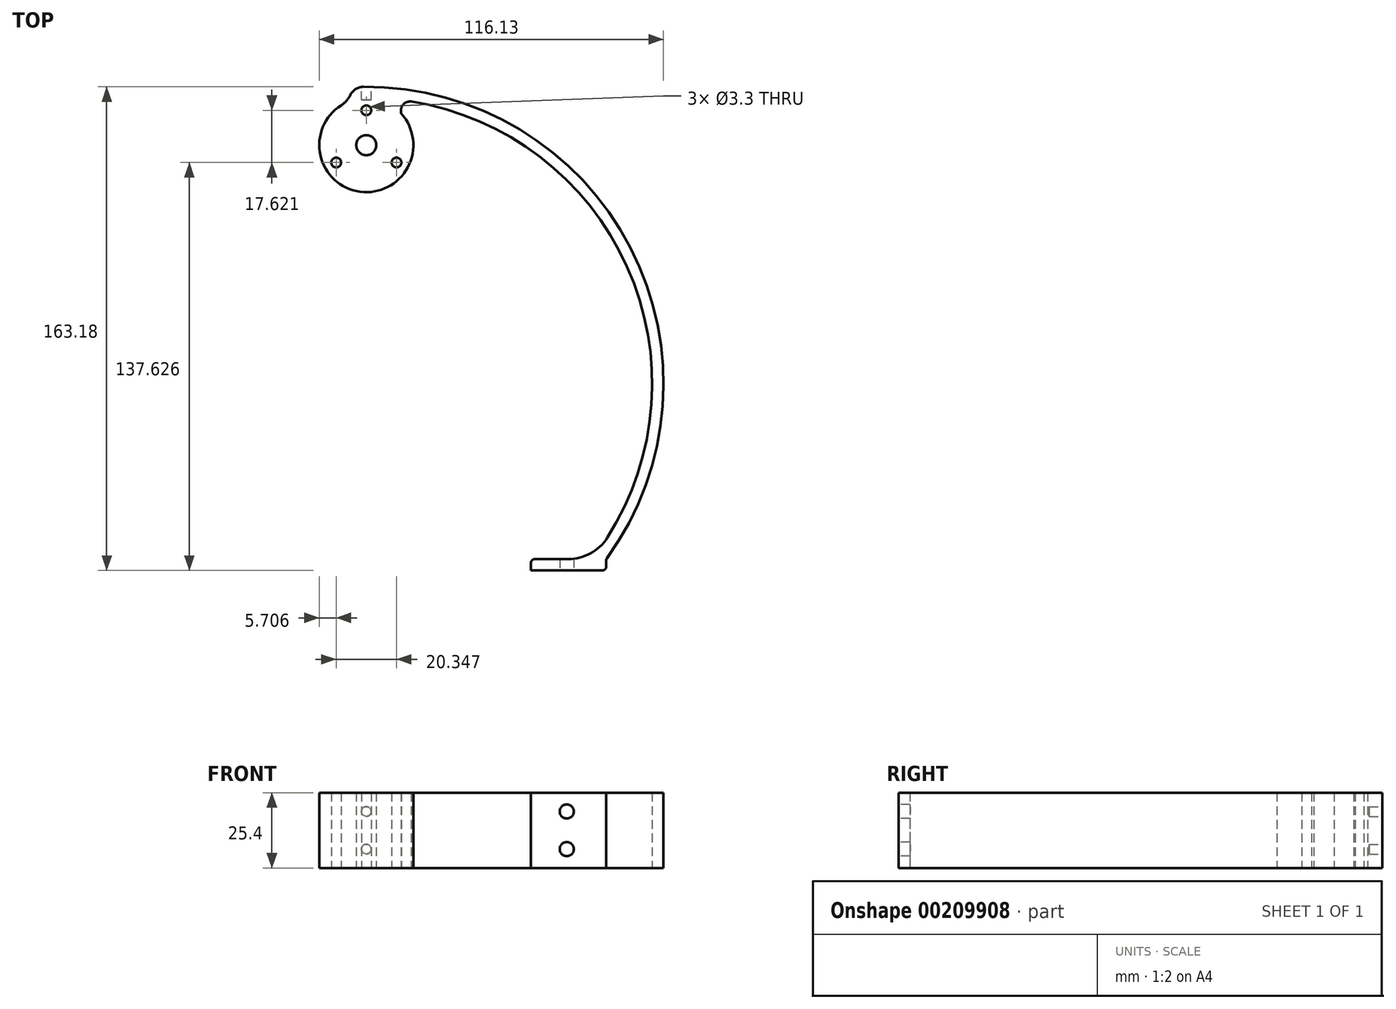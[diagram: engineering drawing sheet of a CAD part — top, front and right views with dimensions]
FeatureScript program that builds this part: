
annotation { "Feature Type Name" : "Feature", "Feature Type Description" : "" }
export const myFeature = defineFeature(function(context is Context, id is Id, definition is map)
    precondition{}
    {
        {
            var Q0;
            Q0=qCreatedBy(makeId("Top.planeOp"),FACE);
            var sketch = newSketch(context, id + "F0", { "sketchPlane" : qUnion([Q0])});
            skCircle(sketch, "E0", {"center": v(0, 0) * mm, "radius": 15.88 * mm});
            skCircle(sketch, "E1", {"center": v(0, 0) * mm, "radius": 3.38 * mm});
            skArc(sketch, "E2", {"start": v(76.2, -139.7) * mm, "mid": v(0, 15.88) * mm, "end": v(-76.2, -139.7) * mm});
            skLineSegment(sketch, "E3", {"start": v(-76.2, -139.7) * mm, "end": v(76.2, -139.7) * mm, "construction": true});
            skLineSegment(sketch, "E4", {"start": v(0, 15.88) * mm, "end": v(0, -139.7) * mm, "construction": true});
            skArc(sketch, "E5.0", {"start": v(81.2, -139.37) * mm, "mid": v(-0.2, 19.67) * mm, "end": v(-80.96, -139.7) * mm});
            skLineSegment(sketch, "E6", {"start": v(56.83, -139.7) * mm, "end": v(80.96, -139.7) * mm, "construction": true});
            skLineSegment(sketch, "E7", {"start": v(76.2, -139.7) * mm, "end": v(55.56, -139.7) * mm});
            skLineSegment(sketch, "E8", {"start": v(55.56, -140.97) * mm, "end": v(55.56, -143.5) * mm});
            skLineSegment(sketch, "E9", {"start": v(55.56, -143.5) * mm, "end": v(79.69, -143.5) * mm});
            skLineSegment(sketch, "E10", {"start": v(80.96, -142.23) * mm, "end": v(80.96, -140.11) * mm});
            skLineSegment(sketch, "E11", {"start": v(0, 19.67) * mm, "end": v(0, 15.88) * mm});
            skLineSegment(sketch, "E12.bottom", {"start": v(0, 26.3) * mm, "end": v(17.78, 26.3) * mm});
            skLineSegment(sketch, "E12.top", {"start": v(0, 22.5) * mm, "end": v(17.78, 22.5) * mm});
            skLineSegment(sketch, "E12.left", {"start": v(0, 26.3) * mm, "end": v(0, 22.5) * mm});
            skLineSegment(sketch, "E12.right", {"start": v(19.05, 25.03) * mm, "end": v(19.05, 23.77) * mm});
            skArc(sketch, "E13", {"start": v(0, 22.5) * mm, "mid": v(-1, 21.09) * mm, "end": v(0, 19.68) * mm});
            skArc(sketch, "E14", {"start": v(0, 26.3) * mm, "mid": v(-4.68, 21.09) * mm, "end": v(0, 15.88) * mm});
            skPoint(sketch, "E15.visualSharp", {"position": v(19.05, 26.3) * mm});
            skArc(sketch, "E15.filletArc", {"start": v(19.05, 25.03) * mm, "mid": v(18.68, 25.93) * mm, "end": v(17.78, 26.3) * mm});
            skPoint(sketch, "E16.visualSharp", {"position": v(19.05, 22.5) * mm});
            skArc(sketch, "E16.filletArc", {"start": v(17.78, 22.5) * mm, "mid": v(18.68, 22.87) * mm, "end": v(19.05, 23.77) * mm});
            skPoint(sketch, "E17.visualSharp", {"position": v(80.96, -143.5) * mm});
            skArc(sketch, "E17.filletArc", {"start": v(79.69, -143.5) * mm, "mid": v(80.58, -143.13) * mm, "end": v(80.96, -142.23) * mm});
            skPoint(sketch, "E18.visualSharp", {"position": v(80.96, -139.7) * mm});
            skArc(sketch, "E18.filletArc", {"start": v(81.2, -139.37) * mm, "mid": v(81.02, -139.72) * mm, "end": v(80.96, -140.11) * mm});
            skPoint(sketch, "E19.newPointB", {"position": v(55.56, -139.7) * mm});
            skArc(sketch, "E19.filletArc", {"start": v(56.83, -139.7) * mm, "mid": v(55.93, -140.07) * mm, "end": v(55.56, -140.97) * mm});
            skLineSegment(sketch, "E20", {"start": v(55.56, -139.7) * mm, "end": v(55.56, -140.97) * mm, "construction": true});
            skLineSegment(sketch, "E21", {"start": v(79.69, -143.5) * mm, "end": v(80.96, -143.5) * mm, "construction": true});
            skLineSegment(sketch, "E22", {"start": v(80.96, -142.23) * mm, "end": v(80.96, -143.5) * mm, "construction": true});
            skArc(sketch, "E23", {"start": v(-8.52, 13.4) * mm, "mid": v(-5.53, 16.7) * mm, "end": v(-4.68, 21.09) * mm});
            skArc(sketch, "E24", {"start": v(15.43, 14.63) * mm, "mid": v(11.9, 12.78) * mm, "end": v(13.1, 8.97) * mm});
            skCircle(sketch, "E25", {"center": v(0, 0) * mm, "radius": 11.75 * mm, "construction": true});
            skCircle(sketch, "E26", {"center": v(0, 11.75) * mm, "radius": 1.65 * mm});
            skCircle(sketch, "E27", {"center": v(10.17, -5.87) * mm, "radius": 1.65 * mm});
            skCircle(sketch, "E28", {"center": v(-10.17, -5.87) * mm, "radius": 1.65 * mm});
            skLineSegment(sketch, "E29", {"start": v(0, 11.75) * mm, "end": v(-10.17, -5.87) * mm, "construction": true});
            skLineSegment(sketch, "E30", {"start": v(10.17, -5.87) * mm, "end": v(0, 11.75) * mm, "construction": true});
            skLineSegment(sketch, "E31", {"start": v(10.17, -5.87) * mm, "end": v(-10.17, -5.87) * mm, "construction": true});
            skLineSegment(sketch, "E32", {"start": v(-10.17, -5.87) * mm, "end": v(5.09, 2.94) * mm, "construction": true});
            skSolve(sketch);
        }
        {
            var Q0;
            {var subQ0=sQuery(id+"F0.wireOp",EDGE,"E24");var subQ1=sQuery(id+"F0.wireOp",EDGE,"E0");var subQ2=makeQuery(id+"F0.imprint","INTERSECT",VERTEX,{"disambiguationData":[OD(0.0)],"derivedFrom":[subQ1,subQ0]});Q0=makeQuery(id+"F0.imprint","IMPRINT",FACE,{"disambiguationData":[TD([[makeQuery(id+"F0.imprint","IMPRINT",EDGE,{"disambiguationData":[TD([[subQ2,-1.0]])],"derivedFrom":subQ1}),1.0]])]});}
            var Q1;
            {var subQ0=sQuery(id+"F0.wireOp",EDGE,"E24");var subQ1=sQuery(id+"F0.wireOp",EDGE,"E2");var subQ2=makeQuery(id+"F0.imprint","INTERSECT",VERTEX,{"disambiguationData":[OD(0.0)],"derivedFrom":[subQ1,subQ0]});Q1=makeQuery(id+"F0.imprint","IMPRINT",FACE,{"disambiguationData":[TD([[makeQuery(id+"F0.imprint","IMPRINT",EDGE,{"disambiguationData":[TD([[subQ2,-1.0]])],"derivedFrom":subQ1}),-1.0]])]});}
            var Q2;
            {var subQ1=sQuery(id+"F0.wireOp",EDGE,"E0");var subQ3=sQuery(id+"F0.wireOp",EDGE,"E24");var subQ4=makeQuery(id+"F0.imprint","INTERSECT",VERTEX,{"disambiguationData":[OD(1.0)],"derivedFrom":[subQ1,subQ3]});Q2=makeQuery(id+"F0.imprint","IMPRINT",FACE,{"disambiguationData":[TD([[makeQuery(id+"F0.imprint","IMPRINT",EDGE,{"disambiguationData":[TD([[subQ4,1.0]])],"derivedFrom":subQ3}),-1.0]])]});}
            var Q3;
            {var subQ1=sQuery(id+"F0.wireOp",EDGE,"E0");var subQ3=sQuery(id+"F0.wireOp",EDGE,"E23");var subQ4=makeQuery(id+"F0.imprint","INTERSECT",VERTEX,{"derivedFrom":[subQ1,subQ3]});Q3=makeQuery(id+"F0.imprint","IMPRINT",FACE,{"disambiguationData":[TD([[makeQuery(id+"F0.imprint","IMPRINT",EDGE,{"disambiguationData":[TD([[subQ4,-1.0]])],"derivedFrom":subQ3}),-1.0]])]});}
            var Q4;
            Q4=makeQuery(id+"F0.imprint","IMPRINT",FACE,{"disambiguationData":[TD([[makeQuery(id+"F0.imprint","IMPRINT",EDGE,{"derivedFrom":sQuery(id+"F0.wireOp",EDGE,"E8")}),1.0]])]});
            var Q5;
            {var subQ3=sQuery(id+"F0.wireOp",EDGE,"E23");var subQ5=sQuery(id+"F0.wireOp",EDGE,"E5.0");var subQ6=makeQuery(id+"F0.imprint","INTERSECT",VERTEX,{"derivedFrom":[subQ5,subQ3]});Q5=makeQuery(id+"F0.imprint","IMPRINT",FACE,{"disambiguationData":[TD([[makeQuery(id+"F0.imprint","IMPRINT",EDGE,{"disambiguationData":[TD([[subQ6,1.0]])],"derivedFrom":subQ5}),1.0]])]});}
            var Q6;
            {var subQ0=sQuery(id+"F0.wireOp",EDGE,"E11");Q6=makeQuery(id+"F0.imprint","IMPRINT",FACE,{"disambiguationData":[TD([[makeQuery(id+"F0.imprint","IMPRINT",EDGE,{"derivedFrom":subQ0}),-1.0]])]});}
            var Q7;
            Q7=makeQuery(id+"F0.imprint","IMPRINT",FACE,{"disambiguationData":[TD([[makeQuery(id+"F0.imprint","IMPRINT",EDGE,{"derivedFrom":sQuery(id+"F0.wireOp",EDGE,"E1")}),-1.0]])]});
            extrude(context, id + "F1", {"entities" : qUnion([Q0, Q1, Q2, Q3, Q4, Q5, Q6, Q7]), "depth" : 25.4 * mm});
        }
        {
            var Q0;
            Q0=qCreatedBy(makeId("Front.planeOp"),FACE);
            cPlane(context, id + "F2", {"entities" : qUnion([Q0]), "cplaneType" : CPlaneType.OFFSET, "offset" : 25.4 * mm, "oppositeDirection" : true, "width" : 152.4 * mm, "height" : 152.4 * mm});
        }
        {
            var Q0;
            Q0=qCreatedBy(id+"F2.planeOp",FACE);
            var sketch = newSketch(context, id + "F3", { "sketchPlane" : qUnion([Q0])});
            skCircle(sketch, "E33", {"center": v(0, 6.35) * mm, "radius": 1.65 * mm});
            skCircle(sketch, "E34", {"center": v(0, 19.05) * mm, "radius": 1.65 * mm});
            skSolve(sketch);
        }
        {
            var Q0;
            Q0 = qSketchRegion(id + "F3", true);
            extrude(context, id + "F4", {"entities" : qUnion([Q0]), "operationType" : NewBodyOperationType.REMOVE, "depth" : 10.16 * mm});
        }
        {
            var Q0;
            Q0=makeQuery(id+"F1.opExtrude","SWEPT_EDGE",EDGE,{"disambiguationData":[OSD([sQuery(id+"F0.wireOp",EDGE,"E5.0"),sQuery(id+"F0.wireOp",EDGE,"E23")])]});
            fillet(context, id + "F5", {"entities" : qUnion([Q0]), "radius" : 5.08 * mm, "tangentPropagation" : true, "allowEdgeOverflow" : false});
        }
        {
            var Q0;
            Q0=makeQuery(id+"F1.opExtrude","SWEPT_EDGE",EDGE,{"disambiguationData":[OSD([sQuery(id+"F0.wireOp",EDGE,"E2"),sQuery(id+"F0.wireOp",EDGE,"E7")])]});
            fillet(context, id + "F6", {"entities" : qUnion([Q0]), "radius" : 15.66 * mm, "tangentPropagation" : true, "allowEdgeOverflow" : false});
        }
        {
            var Q0;
            Q0=makeQuery(id+"F1.opExtrude","SWEPT_FACE",FACE,{"disambiguationData":[OSD([sQuery(id+"F0.wireOp",EDGE,"E9")])]});
            var sketch = newSketch(context, id + "F7", { "sketchPlane" : qUnion([Q0])});
            skLineSegment(sketch, "E35", {"start": v(67.62, 25.4) * mm, "end": v(67.62, 0) * mm, "construction": true});
            skPoint(sketch, "E36", {"position": v(67.62, 19.05) * mm});
            skPoint(sketch, "E37", {"position": v(67.62, 6.35) * mm});
            skSolve(sketch);
        }
        {
            var Q0;
            Q0=sQuery(id+"F7.wireOp",VERTEX,"E36");
            var Q1;
            Q1=sQuery(id+"F7.wireOp",VERTEX,"E37");
            var Q2;
            Q2=makeQuery(id+"F1.opExtrude","SWEPT_BODY",BODY,{"disambiguationData":[OSD([sQuery(id+"F0.wireOp",EDGE,"E0"),sQuery(id+"F0.wireOp",EDGE,"E1"),sQuery(id+"F0.wireOp",EDGE,"E2"),sQuery(id+"F0.wireOp",EDGE,"E5.0"),sQuery(id+"F0.wireOp",EDGE,"E7"),sQuery(id+"F0.wireOp",EDGE,"E8"),sQuery(id+"F0.wireOp",EDGE,"E9"),sQuery(id+"F0.wireOp",EDGE,"E10"),sQuery(id+"F0.wireOp",EDGE,"E12.bottom"),sQuery(id+"F0.wireOp",EDGE,"E12.top"),sQuery(id+"F0.wireOp",EDGE,"E12.right"),sQuery(id+"F0.wireOp",EDGE,"E13"),sQuery(id+"F0.wireOp",EDGE,"E14"),sQuery(id+"F0.wireOp",EDGE,"E15.filletArc"),sQuery(id+"F0.wireOp",EDGE,"E16.filletArc"),sQuery(id+"F0.wireOp",EDGE,"E17.filletArc"),sQuery(id+"F0.wireOp",EDGE,"E18.filletArc"),sQuery(id+"F0.wireOp",EDGE,"E19.filletArc"),sQuery(id+"F0.wireOp",EDGE,"E23"),sQuery(id+"F0.wireOp",EDGE,"E24")])]});
            hole(context, id + "F8", {"style" : HoleStyle.SIMPLE, "endStyle" : HoleEndStyle.BLIND, "holeDiameter" : 4.76 * mm, "holeDepth" : 12.7 * mm, "locations" : qUnion([Q0, Q1]), "scope" : qUnion([Q2])});
        }
    });
